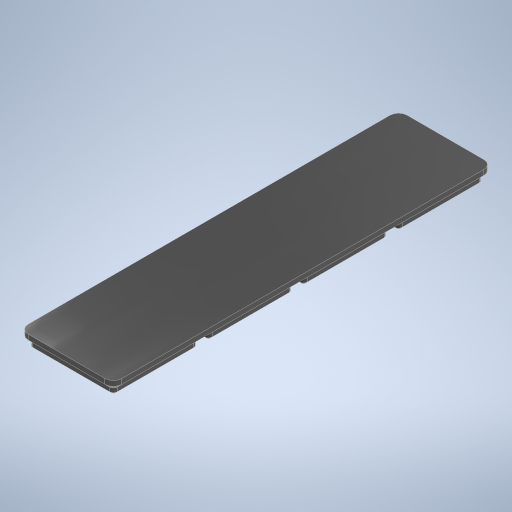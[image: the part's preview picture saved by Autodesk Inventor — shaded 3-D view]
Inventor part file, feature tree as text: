
AUTODESK INVENTOR PART (.ipt)
format: ipt  version: 2023 (Build 270158030, 158C)  size: 423,936 bytes
history: native  units: mm
features: extrude x7, sketch x7, projected_geometry x3, pattern_linear x1
ambient origin geometry x8: Origin, YZ Plane, XZ Plane, XY Plane, X Axis, Y Axis, Z Axis, Center Point
bodies: Solid2 (feature_tree)
feature tree (18):
  extrude  "base-generic"  Depth=41.5mm
  extrude  "Extrusion8"  Depth=2.25mm TaperAngle=0.0deg
  extrude  "Extrusion9"  Depth=2.15mm
  extrude  "Extrusion10"  Depth=0.8mm
  extrude  "Extrusion11"  Depth=7.75mm
  extrude  "Extrusion12"  Depth=7.75mm
  pattern_linear  "Rectangular Pattern1"  Spacing1=2.4mm  [1 undecoded]
  extrude  "fill-gaps"  Depth=3.75mm
  sketch  "Sketch9"  dims[d50=41.5mm d51=41.5mm]
  sketch  "Sketch10"  dims[d52=3.75mm d53=2.25mm d54=0.0mm]
  projected_geometry  "Projected Loop2"
  sketch  "Sketch11"  dims[d55=3.75mm d56=2.15mm d57=-7.853982mm]
  projected_geometry  "Projected Loop3"
  sketch  "Sketch12"  dims[d58=1.8mm d59=0.0mm d60=0.8mm d61=-7.853982mm]
  projected_geometry  "Projected Loop4"
  sketch  "Sketch13"  dims[d62=6.5mm d63=7.75mm]
  sketch  "Sketch14"  dims[d64=7.75mm d65=7.75mm]
  sketch  "Sketch15"  dims[d66=7.75mm d67=2.4mm d68=0.0mm d69=3.0mm d70=6.0mm d71=0.0mm d72=40.0mm d74=42.0mm d75=10.0mm d77=42.0mm d79=2.25mm d80=0.0mm d82=3.75mm d17=0.5mm d18=0.872665mm d19=0.5mm d20=0.872665mm d24=0.0mm d25=0.0mm d26=0.0mm d27=0.0mm]
note: 1 required parameter value undecoded (feature->parameter linkage not recoverable at this tier; creation-order binding heuristic only, values carry confidence <= 0.55)
